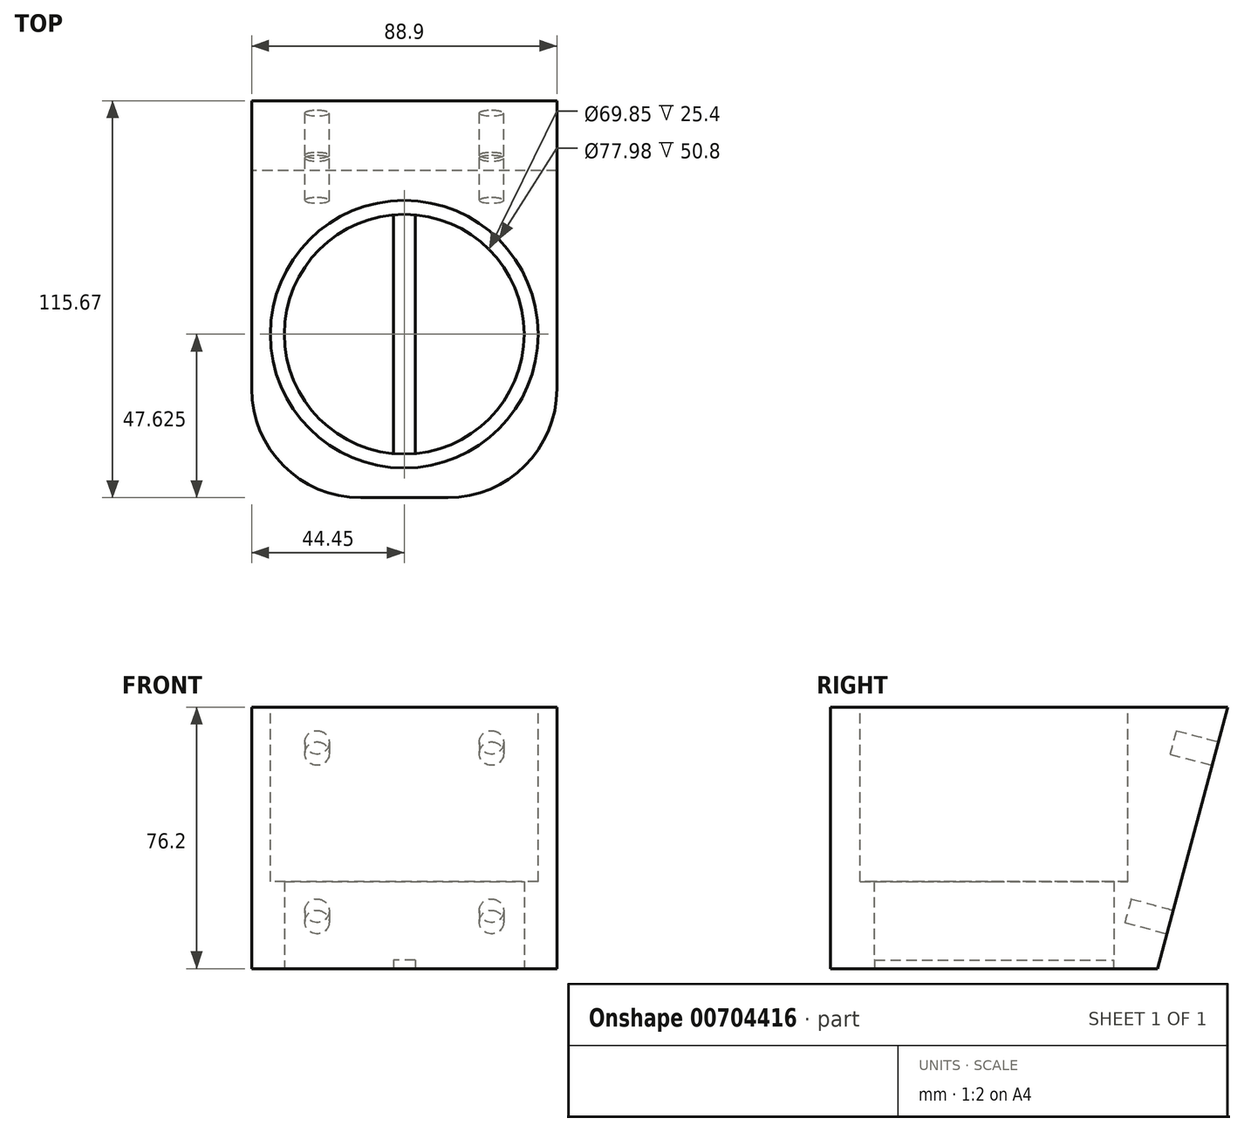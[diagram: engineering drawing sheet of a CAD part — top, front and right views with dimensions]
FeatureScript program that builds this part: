
annotation { "Feature Type Name" : "Feature", "Feature Type Description" : "" }
export const myFeature = defineFeature(function(context is Context, id is Id, definition is map)
    precondition{}
    {
        {
            var Q0;
            Q0=qCreatedBy(makeId("Right.planeOp"),FACE);
            var sketch = newSketch(context, id + "F0", { "sketchPlane" : qUnion([Q0])});
            skLineSegment(sketch, "E0.bottom", {"start": v(0, 0) * mm, "end": v(-88.9, 0) * mm});
            skLineSegment(sketch, "E0.top", {"start": v(0, 76.2) * mm, "end": v(-88.9, 76.2) * mm});
            skLineSegment(sketch, "E0.left", {"start": v(0, 0) * mm, "end": v(0, 76.2) * mm});
            skLineSegment(sketch, "E0.right", {"start": v(-88.9, 0) * mm, "end": v(-88.9, 76.2) * mm});
            skLineSegment(sketch, "E1", {"start": v(0, 0) * mm, "end": v(6.35, 0) * mm});
            skLineSegment(sketch, "E2", {"start": v(6.35, 0) * mm, "end": v(26.77, 76.2) * mm});
            skLineSegment(sketch, "E3", {"start": v(26.77, 76.2) * mm, "end": v(0, 76.2) * mm});
            skSolve(sketch);
        }
        {
            var Q0;
            Q0 = qSketchRegion(id + "F0", true);
            extrude(context, id + "F1", {"entities" : qUnion([Q0]), "depth" : 88.9 * mm, "offsetDistance" : 25.4 * mm});
        }
        {
            var Q0;
            Q0=makeQuery(id+"F1.opExtrude","SWEPT_FACE",FACE,{"disambiguationData":[OSD([sQuery(id+"F0.wireOp",EDGE,"E0.bottom"),sQuery(id+"F0.wireOp",EDGE,"E1")])]});
            var sketch = newSketch(context, id + "F2", { "sketchPlane" : qUnion([Q0])});
            skCircle(sketch, "E4", {"center": v(44.45, 41.28) * mm, "radius": 34.93 * mm});
            skPoint(sketch, "E4.centerSnap0", {"position": v(44.45, 88.9) * mm});
            skPoint(sketch, "E4.centerSnap1", {"position": v(88.9, 41.28) * mm});
            skSolve(sketch);
        }
        {
            var Q0;
            Q0 = qSketchRegion(id + "F2", true);
            extrude(context, id + "F3", {"entities" : qUnion([Q0]), "operationType" : NewBodyOperationType.REMOVE, "oppositeDirection" : true, "depth" : 25.4 * mm, "offsetDistance" : 25.4 * mm});
        }
        {
            var Q0;
            Q0=makeQuery(id+"F1.opExtrude","SWEPT_FACE",FACE,{"disambiguationData":[OSD([sQuery(id+"F0.wireOp",EDGE,"E0.top"),sQuery(id+"F0.wireOp",EDGE,"E3")])]});
            var sketch = newSketch(context, id + "F4", { "sketchPlane" : qUnion([Q0])});
            skCircle(sketch, "E5.0", {"center": v(44.45, -41.28) * mm, "radius": 38.99 * mm});
            skSolve(sketch);
        }
        {
            var Q0;
            Q0 = qSketchRegion(id + "F4", true);
            extrude(context, id + "F5", {"entities" : qUnion([Q0]), "operationType" : NewBodyOperationType.REMOVE, "oppositeDirection" : true, "depth" : 50.8 * mm, "offsetDistance" : 25.4 * mm});
        }
        {
            var Q0;
            Q0=makeQuery(id+"F1.opExtrude","SWEPT_FACE",FACE,{"disambiguationData":[OSD([sQuery(id+"F0.wireOp",EDGE,"E0.bottom"),sQuery(id+"F0.wireOp",EDGE,"E1")])]});
            var sketch = newSketch(context, id + "F6", { "sketchPlane" : qUnion([Q0])});
            skLineSegment(sketch, "E6", {"start": v(44.45, 76.2) * mm, "end": v(44.45, 6.35) * mm, "construction": true});
            skPoint(sketch, "E6.startSnap0", {"position": v(44.45, 88.9) * mm});
            skLineSegment(sketch, "E7", {"start": v(9.52, 41.28) * mm, "end": v(79.38, 41.28) * mm, "construction": true});
            skPoint(sketch, "E7.startSnap0", {"position": v(0, 41.28) * mm});
            skLineSegment(sketch, "E8", {"start": v(9.67, 44.45) * mm, "end": v(79.23, 44.45) * mm});
            skLineSegment(sketch, "E9.MirrorCS", {"start": v(9.67, 38.1) * mm, "end": v(79.23, 38.1) * mm});
            skLineSegment(sketch, "E10", {"start": v(41.27, 76.06) * mm, "end": v(41.28, 6.5) * mm});
            skLineSegment(sketch, "E11.MirrorCS", {"start": v(47.62, 76.06) * mm, "end": v(47.63, 6.5) * mm});
            skSolve(sketch);
        }
        {
            var Q0;
            {var subQ0=sQuery(id+"F6.wireOp",EDGE,"E8");var subQ1=makeQuery(id+"F3.boolean.opBoolean","COPY",EDGE,{"derivedFrom":makeQuery(id+"F3.opExtrude","CAP_EDGE",EDGE,{"disambiguationData":[OSD([sQuery(id+"F2.wireOp",EDGE,"E4")])],"isStart":true})});var subQ2=makeQuery(id+"F6.imprint","INTERSECT",VERTEX,{"disambiguationData":[OD(0.0)],"derivedFrom":[subQ1,subQ0]});Q0=makeQuery(id+"F6.imprint","IMPRINT",FACE,{"disambiguationData":[TD([[makeQuery(id+"F6.imprint","IMPRINT",EDGE,{"disambiguationData":[TD([[subQ2,-1.0]])],"derivedFrom":subQ0}),-1.0]])]});}
            var Q1;
            {var subQ0=sQuery(id+"F6.wireOp",EDGE,"E10");var subQ1=sQuery(id+"F6.wireOp",EDGE,"E8");var subQ2=makeQuery(id+"F6.imprint","INTERSECT",VERTEX,{"derivedFrom":[subQ1,subQ0]});Q1=makeQuery(id+"F6.imprint","IMPRINT",FACE,{"disambiguationData":[TD([[makeQuery(id+"F6.imprint","IMPRINT",EDGE,{"disambiguationData":[TD([[subQ2,-1.0]])],"derivedFrom":subQ1}),1.0]])]});}
            var Q2;
            {var subQ0=sQuery(id+"F6.wireOp",EDGE,"E8");var subQ1=makeQuery(id+"F3.boolean.opBoolean","COPY",EDGE,{"derivedFrom":makeQuery(id+"F3.opExtrude","CAP_EDGE",EDGE,{"disambiguationData":[OSD([sQuery(id+"F2.wireOp",EDGE,"E4")])],"isStart":true})});var subQ2=makeQuery(id+"F6.imprint","INTERSECT",VERTEX,{"disambiguationData":[OD(1.0)],"derivedFrom":[subQ1,subQ0]});Q2=makeQuery(id+"F6.imprint","IMPRINT",FACE,{"disambiguationData":[TD([[makeQuery(id+"F6.imprint","IMPRINT",EDGE,{"disambiguationData":[TD([[subQ2,1.0]])],"derivedFrom":subQ0}),-1.0]])]});}
            var Q3;
            {var subQ0=sQuery(id+"F6.wireOp",EDGE,"E10");var subQ1=sQuery(id+"F6.wireOp",EDGE,"E8");var subQ2=makeQuery(id+"F6.imprint","INTERSECT",VERTEX,{"derivedFrom":[subQ1,subQ0]});Q3=makeQuery(id+"F6.imprint","IMPRINT",FACE,{"disambiguationData":[TD([[makeQuery(id+"F6.imprint","IMPRINT",EDGE,{"disambiguationData":[TD([[subQ2,-1.0]])],"derivedFrom":subQ1}),-1.0]])]});}
            var Q4;
            {var subQ0=sQuery(id+"F6.wireOp",EDGE,"E10");var subQ1=sQuery(id+"F6.wireOp",EDGE,"E9.MirrorCS");var subQ2=makeQuery(id+"F6.imprint","INTERSECT",VERTEX,{"derivedFrom":[subQ1,subQ0]});Q4=makeQuery(id+"F6.imprint","IMPRINT",FACE,{"disambiguationData":[TD([[makeQuery(id+"F6.imprint","IMPRINT",EDGE,{"disambiguationData":[TD([[subQ2,-1.0]])],"derivedFrom":subQ1}),-1.0]])]});}
            extrude(context, id + "F7", {"entities" : qUnion([Q0, Q1, Q2, Q3, Q4]), "operationType" : NewBodyOperationType.ADD, "oppositeDirection" : true, "depth" : 2.54 * mm, "offsetDistance" : 25.4 * mm});
        }
        {
            var Q0;
            Q0=makeQuery(id+"F1.opExtrude","SWEPT_FACE",FACE,{"disambiguationData":[OSD([sQuery(id+"F0.wireOp",EDGE,"E2")])]});
            var sketch = newSketch(context, id + "F8", { "sketchPlane" : qUnion([Q0])});
            skLineSegment(sketch, "E12", {"start": v(-44.45, 80.53) * mm, "end": v(-44.45, 1.64) * mm, "construction": true});
            skLineSegment(sketch, "E13", {"start": v(-88.9, 41.09) * mm, "end": v(0, 41.09) * mm, "construction": true});
            skCircle(sketch, "E14", {"center": v(-69.85, 66.49) * mm, "radius": 3.56 * mm});
            skCircle(sketch, "E15.MirrorC", {"center": v(-19.05, 66.49) * mm, "radius": 3.56 * mm});
            skCircle(sketch, "E16.MirrorC", {"center": v(-69.85, 15.69) * mm, "radius": 3.56 * mm});
            skCircle(sketch, "E17.MirrorC", {"center": v(-19.05, 15.69) * mm, "radius": 3.56 * mm});
            skSolve(sketch);
        }
        {
            var Q0;
            Q0 = qSketchRegion(id + "F8", true);
            extrude(context, id + "F9", {"entities" : qUnion([Q0]), "operationType" : NewBodyOperationType.REMOVE, "oppositeDirection" : true, "depth" : 12.7 * mm, "offsetDistance" : 25.4 * mm});
        }
        {
            var Q0;
            Q0=makeQuery(id+"F1.opExtrude","CAP_EDGE",EDGE,{"disambiguationData":[OSD([sQuery(id+"F0.wireOp",EDGE,"E0.right")])],"isStart":true});
            var Q1;
            Q1=makeQuery(id+"F1.opExtrude","CAP_EDGE",EDGE,{"disambiguationData":[OSD([sQuery(id+"F0.wireOp",EDGE,"E0.right")])],"isStart":false});
            fillet(context, id + "F10", {"entities" : qUnion([Q0, Q1]), "tangentPropagation" : true, "radius" : 31.75 * mm, "defaultsChanged" : true, "vertexSettings" : [], "allowEdgeOverflow" : false});
        }
    });
